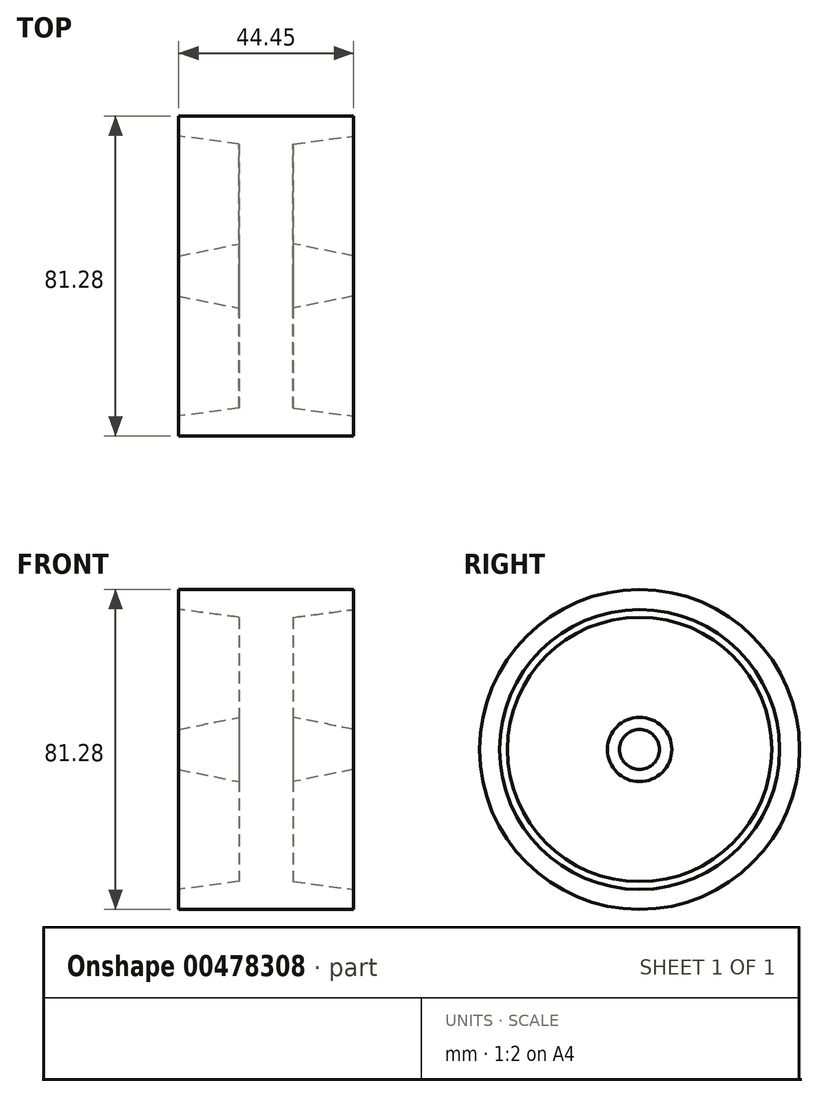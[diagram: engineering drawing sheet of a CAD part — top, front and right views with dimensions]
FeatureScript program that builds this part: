
annotation { "Feature Type Name" : "Feature", "Feature Type Description" : "" }
export const myFeature = defineFeature(function(context is Context, id is Id, definition is map)
    precondition{}
    {
        {
            var Q0;
            Q0=qCreatedBy(makeId("Top.planeOp"),FACE);
            var sketch = newSketch(context, id + "F0", { "sketchPlane" : qUnion([Q0])});
            skLineSegment(sketch, "E0", {"start": v(0, 0) * mm, "end": v(44.45, 0) * mm});
            skLineSegment(sketch, "E1", {"start": v(44.45, 0) * mm, "end": v(44.45, -5.08) * mm});
            skLineSegment(sketch, "E2", {"start": v(44.45, -5.08) * mm, "end": v(29.1, -8.18) * mm});
            skLineSegment(sketch, "E3", {"start": v(29.1, -8.18) * mm, "end": v(29.1, -33.58) * mm});
            skLineSegment(sketch, "E4", {"start": v(29.1, -33.58) * mm, "end": v(44.45, -35.56) * mm});
            skLineSegment(sketch, "E5", {"start": v(44.45, -35.56) * mm, "end": v(44.45, -40.64) * mm});
            skLineSegment(sketch, "E6", {"start": v(44.45, -40.64) * mm, "end": v(0, -40.64) * mm});
            skLineSegment(sketch, "E7", {"start": v(0, -40.64) * mm, "end": v(0, -35.56) * mm});
            skLineSegment(sketch, "E8", {"start": v(0, -35.56) * mm, "end": v(15.35, -33.58) * mm});
            skLineSegment(sketch, "E9", {"start": v(15.35, -33.58) * mm, "end": v(15.35, -8.18) * mm});
            skLineSegment(sketch, "E10", {"start": v(15.35, -8.18) * mm, "end": v(0, -5.08) * mm});
            skLineSegment(sketch, "E11", {"start": v(0, -5.08) * mm, "end": v(0, 0) * mm});
            skSolve(sketch);
        }
        {
            var Q0;
            Q0=qCreatedBy(makeId("Right.planeOp"),FACE);
            var sketch = newSketch(context, id + "F1", { "sketchPlane" : qUnion([Q0])});
            skCircle(sketch, "E12", {"center": v(0, 0) * mm, "radius": 32.46 * mm});
            skSolve(sketch);
        }
        {
            var Q0;
            Q0=makeQuery(id+"F0.imprint","IMPRINT",FACE,{"disambiguationData":[TD([[makeQuery(id+"F0.imprint","IMPRINT",EDGE,{"derivedFrom":sQuery(id+"F0.wireOp",EDGE,"E0")}),-1.0]])]});
            var Q1;
            Q1=sQuery(id+"F1.wireOp",EDGE,"E12");
            revolve(context, id + "F2", {"entities" : qUnion([Q0]), "axis" : qUnion([Q1]), "revolveType" : RevolveType.FULL});
        }
    });
